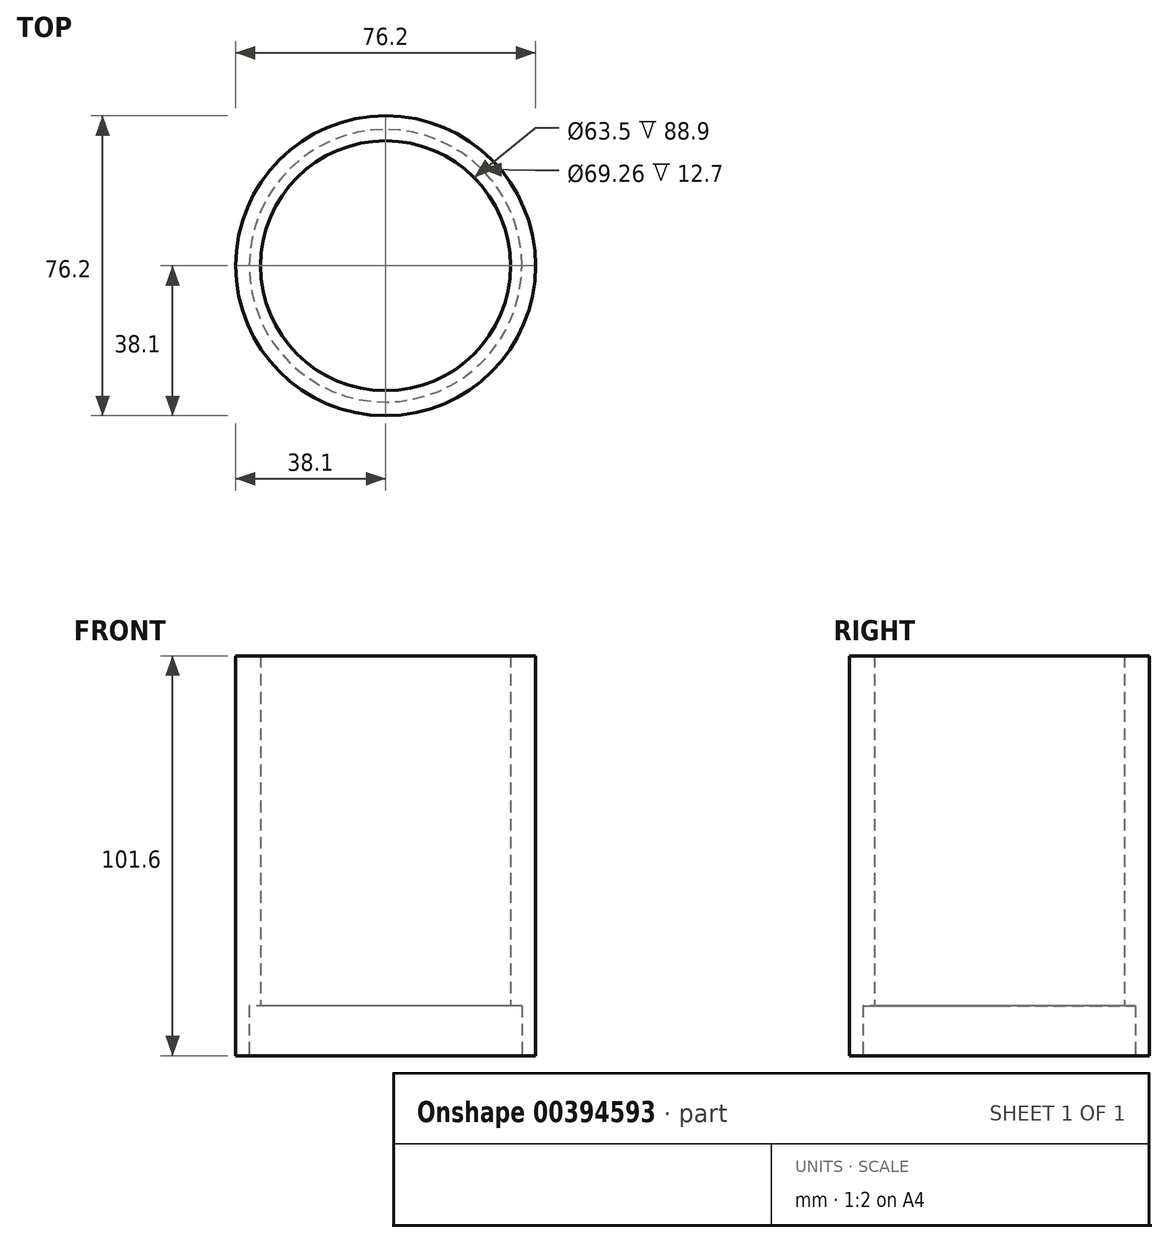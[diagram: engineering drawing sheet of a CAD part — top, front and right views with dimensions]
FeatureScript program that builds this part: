
annotation { "Feature Type Name" : "Feature", "Feature Type Description" : "" }
export const myFeature = defineFeature(function(context is Context, id is Id, definition is map)
    precondition{}
    {
        {
            var Q0;
            Q0=qCreatedBy(makeId("Top.planeOp"),FACE);
            var sketch = newSketch(context, id + "F0", { "sketchPlane" : qUnion([Q0])});
            skCircle(sketch, "E0", {"center": v(0, 0) * mm, "radius": 38.1 * mm});
            skCircle(sketch, "E1", {"center": v(0, 0) * mm, "radius": 31.75 * mm});
            skSolve(sketch);
        }
        {
            var Q0;
            Q0 = qSketchRegion(id + "F0", true);
            extrude(context, id + "F1", {"entities" : qUnion([Q0]), "depth" : 101.6 * mm});
        }
        {
            var Q0;
            Q0=qCreatedBy(makeId("Top.planeOp"),FACE);
            var sketch = newSketch(context, id + "F2", { "sketchPlane" : qUnion([Q0])});
            skCircle(sketch, "E2", {"center": v(0, 0) * mm, "radius": 34.63 * mm});
            skSolve(sketch);
        }
        {
            var Q0;
            Q0 = qSketchRegion(id + "F2", true);
            extrude(context, id + "F3", {"entities" : qUnion([Q0]), "operationType" : NewBodyOperationType.REMOVE, "depth" : 12.7 * mm});
        }
    });
